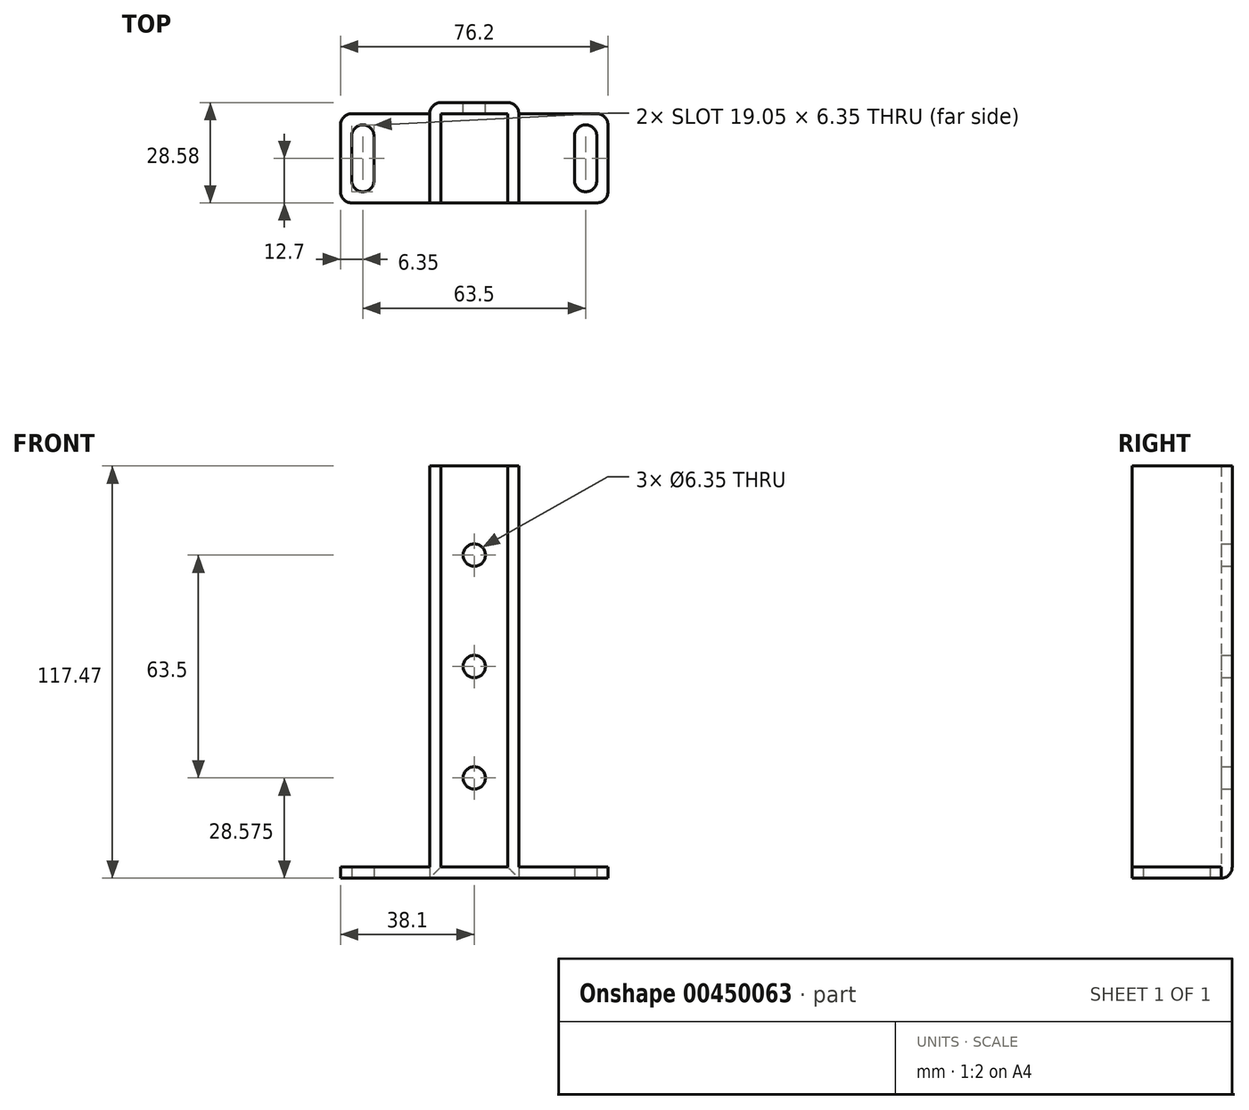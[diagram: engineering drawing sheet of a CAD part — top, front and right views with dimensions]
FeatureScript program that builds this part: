
annotation { "Feature Type Name" : "Feature", "Feature Type Description" : "" }
export const myFeature = defineFeature(function(context is Context, id is Id, definition is map)
    precondition{}
    {
        {
            var Q0;
            Q0=qCreatedBy(makeId("Top.planeOp"),FACE);
            var sketch = newSketch(context, id + "F0", { "sketchPlane" : qUnion([Q0])});
            skLineSegment(sketch, "E0.bottom", {"start": v(-34.93, 12.7) * mm, "end": v(34.92, 12.7) * mm});
            skLineSegment(sketch, "E0.top", {"start": v(-34.93, -12.7) * mm, "end": v(34.92, -12.7) * mm});
            skLineSegment(sketch, "E0.left", {"start": v(-38.1, 9.53) * mm, "end": v(-38.1, -9.52) * mm});
            skLineSegment(sketch, "E0.right", {"start": v(38.1, 9.53) * mm, "end": v(38.1, -9.52) * mm});
            skPoint(sketch, "E0.middle", {"position": v(0, 0) * mm});
            skPoint(sketch, "E1.visualSharp", {"position": v(-38.1, 12.7) * mm});
            skArc(sketch, "E1.filletArc", {"start": v(-34.93, 12.7) * mm, "mid": v(-37.17, 11.77) * mm, "end": v(-38.1, 9.53) * mm});
            skPoint(sketch, "E2.visualSharp", {"position": v(38.1, 12.7) * mm});
            skArc(sketch, "E2.filletArc", {"start": v(38.1, 9.53) * mm, "mid": v(37.17, 11.77) * mm, "end": v(34.92, 12.7) * mm});
            skPoint(sketch, "E3.visualSharp", {"position": v(38.1, -12.7) * mm});
            skArc(sketch, "E3.filletArc", {"start": v(34.92, -12.7) * mm, "mid": v(37.17, -11.77) * mm, "end": v(38.1, -9.52) * mm});
            skPoint(sketch, "E4.visualSharp", {"position": v(-38.1, -12.7) * mm});
            skArc(sketch, "E4.filletArc", {"start": v(-38.1, -9.52) * mm, "mid": v(-37.17, -11.77) * mm, "end": v(-34.93, -12.7) * mm});
            skLineSegment(sketch, "E5", {"start": v(-31.75, 6.35) * mm, "end": v(-31.75, -6.35) * mm});
            skLineSegment(sketch, "E6.MirrorCS", {"start": v(31.75, 6.35) * mm, "end": v(31.75, -6.35) * mm});
            skArc(sketch, "E7.0.startCap", {"start": v(-34.92, 6.35) * mm, "mid": v(-31.75, 9.52) * mm, "end": v(-28.58, 6.35) * mm});
            skArc(sketch, "E7.0.endCap", {"start": v(-28.57, -6.35) * mm, "mid": v(-31.75, -9.53) * mm, "end": v(-34.92, -6.35) * mm});
            skLineSegment(sketch, "E7.0.left", {"start": v(-28.57, 6.35) * mm, "end": v(-28.57, -6.35) * mm});
            skLineSegment(sketch, "E7.0.right", {"start": v(-34.92, 6.35) * mm, "end": v(-34.92, -6.35) * mm});
            skArc(sketch, "E7.1.startCap", {"start": v(28.57, 6.35) * mm, "mid": v(31.75, 9.53) * mm, "end": v(34.92, 6.35) * mm});
            skArc(sketch, "E7.1.endCap", {"start": v(34.92, -6.35) * mm, "mid": v(31.75, -9.52) * mm, "end": v(28.58, -6.35) * mm});
            skLineSegment(sketch, "E7.1.left", {"start": v(34.92, 6.35) * mm, "end": v(34.92, -6.35) * mm});
            skLineSegment(sketch, "E7.1.right", {"start": v(28.57, 6.35) * mm, "end": v(28.57, -6.35) * mm});
            skSolve(sketch);
        }
        {
            var Q0;
            Q0=makeQuery(id+"F0.imprint","IMPRINT",FACE,{"disambiguationData":[TD([[makeQuery(id+"F0.imprint","IMPRINT",EDGE,{"derivedFrom":sQuery(id+"F0.wireOp",EDGE,"E0.bottom")}),-1.0]])]});
            extrude(context, id + "F1", {"entities" : qUnion([Q0]), "depth" : 3.17 * mm, "offsetDistance" : 25.4 * mm});
        }
        {
            var Q0;
            Q0=makeQuery(id+"F1.opExtrude","CAP_FACE",FACE,{"disambiguationData":[OSD([sQuery(id+"F0.wireOp",EDGE,"E0.bottom"),sQuery(id+"F0.wireOp",EDGE,"E0.top"),sQuery(id+"F0.wireOp",EDGE,"E0.left"),sQuery(id+"F0.wireOp",EDGE,"E0.right"),sQuery(id+"F0.wireOp",EDGE,"E1.filletArc"),sQuery(id+"F0.wireOp",EDGE,"E2.filletArc"),sQuery(id+"F0.wireOp",EDGE,"E3.filletArc"),sQuery(id+"F0.wireOp",EDGE,"E4.filletArc"),sQuery(id+"F0.wireOp",EDGE,"E7.0.startCap"),sQuery(id+"F0.wireOp",EDGE,"E7.0.endCap"),sQuery(id+"F0.wireOp",EDGE,"E7.0.left"),sQuery(id+"F0.wireOp",EDGE,"E7.0.right"),sQuery(id+"F0.wireOp",EDGE,"E7.1.startCap"),sQuery(id+"F0.wireOp",EDGE,"E7.1.endCap"),sQuery(id+"F0.wireOp",EDGE,"E7.1.left"),sQuery(id+"F0.wireOp",EDGE,"E7.1.right")])],"isStart":false});
            var sketch = newSketch(context, id + "F2", { "sketchPlane" : qUnion([Q0])});
            skLineSegment(sketch, "E8", {"start": v(12.7, -12.7) * mm, "end": v(12.7, 15.88) * mm});
            skLineSegment(sketch, "E9", {"start": v(12.7, 15.88) * mm, "end": v(-12.7, 15.88) * mm});
            skLineSegment(sketch, "E10", {"start": v(-12.7, 15.88) * mm, "end": v(-12.7, -12.7) * mm});
            skPoint(sketch, "E11", {"position": v(0, 15.88) * mm});
            skLineSegment(sketch, "E12.0", {"start": v(-9.53, 12.7) * mm, "end": v(-9.53, -12.7) * mm});
            skLineSegment(sketch, "E12.1", {"start": v(9.52, 12.7) * mm, "end": v(-9.52, 12.7) * mm});
            skLineSegment(sketch, "E12.2", {"start": v(9.53, -12.7) * mm, "end": v(9.53, 12.7) * mm});
            skSolve(sketch);
        }
        {
            var Q0;
            {var subQ5=sQuery(id+"F2.wireOp",EDGE,"E12.2");Q0=makeQuery(id+"F2.imprint","IMPRINT",FACE,{"disambiguationData":[TD([[makeQuery(id+"F2.imprint","IMPRINT",EDGE,{"derivedFrom":subQ5}),-1.0]])]});}
            var Q1;
            {var subQ5=sQuery(id+"F2.wireOp",EDGE,"E12.0");Q1=makeQuery(id+"F2.imprint","IMPRINT",FACE,{"disambiguationData":[TD([[makeQuery(id+"F2.imprint","IMPRINT",EDGE,{"derivedFrom":subQ5}),-1.0]])]});}
            extrude(context, id + "F3", {"entities" : qUnion([Q0, Q1]), "operationType" : NewBodyOperationType.ADD, "depth" : 114.3 * mm, "offsetDistance" : 25.4 * mm});
        }
        {
            var Q0;
            {var subQ1=sQuery(id+"F0.wireOp",EDGE,"E0.bottom");var subQ2=makeQuery(id+"F1.opExtrude","CAP_EDGE",EDGE,{"disambiguationData":[OSD([subQ1])],"isStart":false});Q0=makeQuery(id+"F3.boolean.opBoolean","MERGE",FACE,{"derivedFrom":[makeQuery(id+"F1.opExtrude","SWEPT_FACE",FACE,{"disambiguationData":[OSD([subQ1])]}),makeQuery(id+"F3.opExtrude","SWEPT_FACE",FACE,{"disambiguationData":[OSD([subQ1]),TDD([makeQuery(id+"F2.imprint","IMPRINT",EDGE,{"disambiguationData":[TD([[makeQuery(id+"F2.imprint","INTERSECT",VERTEX,{"derivedFrom":[subQ2,sQuery(id+"F2.wireOp",EDGE,"E10")]}),-1.0]])],"derivedFrom":subQ2})])]}),makeQuery(id+"F3.opExtrude","SWEPT_FACE",FACE,{"disambiguationData":[OSD([subQ1]),TDD([makeQuery(id+"F2.imprint","IMPRINT",EDGE,{"disambiguationData":[TD([[makeQuery(id+"F2.imprint","INTERSECT",VERTEX,{"derivedFrom":[subQ2,sQuery(id+"F2.wireOp",EDGE,"E8")]}),1.0]])],"derivedFrom":subQ2})])]})]});}
            var sketch = newSketch(context, id + "F4", { "sketchPlane" : qUnion([Q0])});
            skLineSegment(sketch, "E13.0", {"start": v(-12.7, 117.48) * mm, "end": v(-12.7, 3.18) * mm});
            skLineSegment(sketch, "E14.0", {"start": v(34.93, 0) * mm, "end": v(-34.92, 0) * mm});
            skLineSegment(sketch, "E15.0", {"start": v(12.7, 117.48) * mm, "end": v(12.7, 0) * mm});
            skPoint(sketch, "E16.orphan", {"position": v(-12.7, 3.18) * mm});
            skPoint(sketch, "E17.orphan", {"position": v(12.7, 3.18) * mm});
            skLineSegment(sketch, "E18.0", {"start": v(9.53, 117.48) * mm, "end": v(-12.7, 117.48) * mm});
            skLineSegment(sketch, "E19.0", {"start": v(12.7, 117.48) * mm, "end": v(9.53, 117.48) * mm});
            skPoint(sketch, "E20.orphan", {"position": v(-9.52, 117.48) * mm});
            skPoint(sketch, "E21", {"position": v(0, 28.58) * mm});
            skPoint(sketch, "E22", {"position": v(0, 60.33) * mm});
            skPoint(sketch, "E23", {"position": v(0, 92.08) * mm});
            skLineSegment(sketch, "E24", {"start": v(-12.7, 3.17) * mm, "end": v(-9.52, 3.18) * mm});
            skLineSegment(sketch, "E25", {"start": v(-9.52, 3.18) * mm, "end": v(-9.52, 0) * mm});
            skLineSegment(sketch, "E26", {"start": v(9.53, 3.17) * mm, "end": v(12.7, 3.18) * mm});
            skLineSegment(sketch, "E27", {"start": v(9.53, 3.18) * mm, "end": v(9.53, 0) * mm});
            skLineSegment(sketch, "E28", {"start": v(-12.7, 3.18) * mm, "end": v(-12.7, 0) * mm});
            skSolve(sketch);
        }
        {
            var Q0;
            {var subQ3=sQuery(id+"F4.wireOp",EDGE,"E24");Q0=makeQuery(id+"F4.imprint","IMPRINT",FACE,{"disambiguationData":[TD([[makeQuery(id+"F4.imprint","IMPRINT",EDGE,{"derivedFrom":subQ3}),1.0]])]});}
            var Q1;
            {var subQ1=sQuery(id+"F2.wireOp",EDGE,"E12.1");var subQ2=sQuery(id+"F2.wireOp",EDGE,"E12.0");var subQ3=sQuery(id+"F0.wireOp",EDGE,"E0.bottom");var subQ4=makeQuery(id+"F3.opExtrude","SWEPT_EDGE",EDGE,{"disambiguationData":[OSD([subQ3,subQ2,subQ1])]});Q1=makeQuery(id+"F4.imprint","IMPRINT",FACE,{"disambiguationData":[TD([[makeQuery(id+"F4.imprint","IMPRINT",EDGE,{"derivedFrom":subQ4}),-1.0]])]});}
            var Q2;
            {var subQ0=sQuery(id+"F4.wireOp",EDGE,"E19.0");Q2=makeQuery(id+"F4.imprint","IMPRINT",FACE,{"disambiguationData":[TD([[makeQuery(id+"F4.imprint","IMPRINT",EDGE,{"derivedFrom":subQ0}),1.0]])]});}
            var Q3;
            {var subQ0=sQuery(id+"F4.wireOp",EDGE,"E25");Q3=makeQuery(id+"F4.imprint","IMPRINT",FACE,{"disambiguationData":[TD([[makeQuery(id+"F4.imprint","IMPRINT",EDGE,{"derivedFrom":subQ0}),1.0]])]});}
            var Q4;
            Q4=makeQuery(id+"F4.imprint","IMPRINT",FACE,{"disambiguationData":[TD([[makeQuery(id+"F4.imprint","IMPRINT",EDGE,{"derivedFrom":sQuery(id+"F4.wireOp",EDGE,"E24")}),-1.0]])]});
            var Q5;
            {var subQ4=sQuery(id+"F4.wireOp",EDGE,"E26");Q5=makeQuery(id+"F4.imprint","IMPRINT",FACE,{"disambiguationData":[TD([[makeQuery(id+"F4.imprint","IMPRINT",EDGE,{"derivedFrom":subQ4}),-1.0]])]});}
            extrude(context, id + "F5", {"entities" : qUnion([Q0, Q1, Q2, Q3, Q4, Q5]), "operationType" : NewBodyOperationType.ADD, "depth" : 3.17 * mm, "offsetDistance" : 25.4 * mm});
        }
        {
            var Q0;
            Q0=sQuery(id+"F4.wireOp",VERTEX,"E21");
            var Q1;
            Q1=sQuery(id+"F4.wireOp",VERTEX,"E22");
            var Q2;
            Q2=sQuery(id+"F4.wireOp",VERTEX,"E23");
            var Q3;
            Q3=makeQuery(id+"F1.opExtrude","SWEPT_BODY",BODY,{"disambiguationData":[OSD([sQuery(id+"F0.wireOp",EDGE,"E0.bottom"),sQuery(id+"F0.wireOp",EDGE,"E0.top"),sQuery(id+"F0.wireOp",EDGE,"E0.left"),sQuery(id+"F0.wireOp",EDGE,"E0.right"),sQuery(id+"F0.wireOp",EDGE,"E1.filletArc"),sQuery(id+"F0.wireOp",EDGE,"E2.filletArc"),sQuery(id+"F0.wireOp",EDGE,"E3.filletArc"),sQuery(id+"F0.wireOp",EDGE,"E4.filletArc"),sQuery(id+"F0.wireOp",EDGE,"E7.0.startCap"),sQuery(id+"F0.wireOp",EDGE,"E7.0.endCap"),sQuery(id+"F0.wireOp",EDGE,"E7.0.left"),sQuery(id+"F0.wireOp",EDGE,"E7.0.right"),sQuery(id+"F0.wireOp",EDGE,"E7.1.startCap"),sQuery(id+"F0.wireOp",EDGE,"E7.1.endCap"),sQuery(id+"F0.wireOp",EDGE,"E7.1.left"),sQuery(id+"F0.wireOp",EDGE,"E7.1.right")])]});
            hole(context, id + "F6", {"style" : HoleStyle.SIMPLE, "endStyle" : HoleEndStyle.THROUGH, "oppositeDirection" : true, "holeDiameter" : 6.35 * mm, "isTappedThrough" : true, "tappedDepth" : 12.7 * mm, "tapClearance" : 3, "locations" : qUnion([Q0, Q1, Q2]), "scope" : qUnion([Q3]), "startStyle" : HoleStartStyle.PART});
        }
        {
            var Q0;
            Q0=makeQuery(id+"F5.opExtrude","CAP_EDGE",EDGE,{"disambiguationData":[OSD([sQuery(id+"F4.wireOp",EDGE,"E14.0")])],"isStart":false});
            var Q1;
            Q1=makeQuery(id+"F5.opExtrude","CAP_EDGE",EDGE,{"disambiguationData":[OSD([sQuery(id+"F4.wireOp",EDGE,"E13.0"),sQuery(id+"F4.wireOp",EDGE,"E28")])],"isStart":false});
            var Q2;
            Q2=makeQuery(id+"F5.opExtrude","CAP_EDGE",EDGE,{"disambiguationData":[OSD([sQuery(id+"F4.wireOp",EDGE,"E15.0")])],"isStart":false});
            fillet(context, id + "F7", {"entities" : qUnion([Q0, Q1, Q2]), "radius" : 3.17 * mm, "tangentPropagation" : true, "allowEdgeOverflow" : false});
        }
    });
